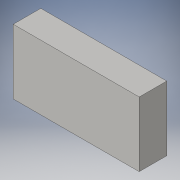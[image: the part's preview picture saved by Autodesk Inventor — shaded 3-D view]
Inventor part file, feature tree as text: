
AUTODESK INVENTOR PART (.ipt)
format: ipt  version: 2016 (Build 200138000, 138)  size: 82,432 bytes
history: native  units: in
note: dims shown in document units (in); Inventor stores cm internally (conversion verified against a paired STEP export)
features: extrude x1, sketch x1
ambient origin geometry x8: Origin, YZ Plane, XZ Plane, XY Plane, X Axis, Y Axis, Z Axis, Center Point
bodies: Solid1 (feature_tree)
feature tree (2):
  extrude  "Extrusion1"  Depth=2.284in
  sketch  "Sketch1"  dims[d0=1.173in d1=2.284in d2=0.5in d3=0.0in]
